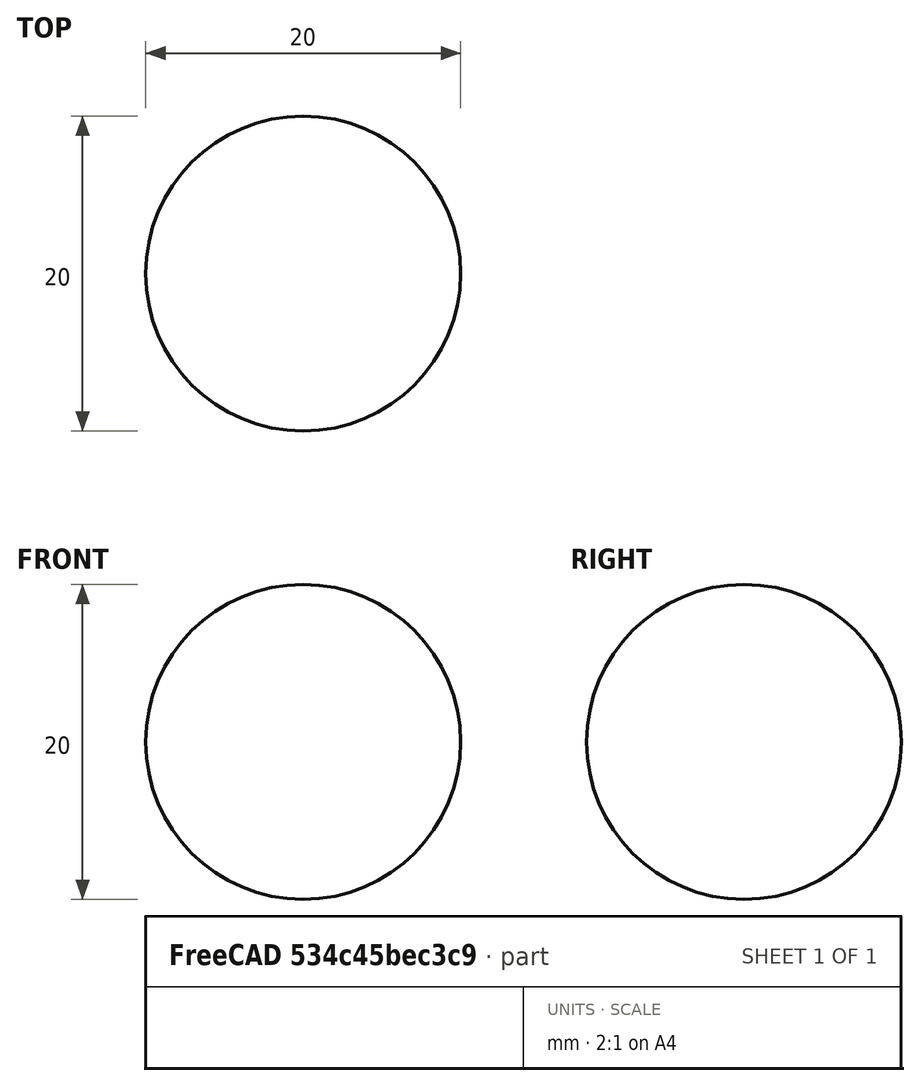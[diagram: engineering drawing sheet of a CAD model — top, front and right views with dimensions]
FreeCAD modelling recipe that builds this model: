
FCSTD DOCUMENT  (FreeCAD 0.18R14555 (Git shallow))
Label: CURVA DE VIVIANI
License: All rights reserved
LicenseURL: http://en.wikipedia.org/wiki/All_rights_reserved
objects: App::DocumentObjectGroupPython×2, Part::Feature×1, Part::Sphere×1
note: 2 computed .brp shape members not serialized (recipe doc carries the construction recipe); baked Part::Feature solids carry a one-line shape summary decoded from their .brp

FEATURE [Part::Feature] Wire
  shape: bbox 100 x 100.2 x 200 mm, 0 faces, 0 solids (baked)
FEATURE [Part::Sphere] Sphere
  Angle1 = -90
  Angle2 = 90
  Angle3 = 360
  AttacherType = Attacher::AttachEngine3D
  Placement = pos=(100,0,0) rot=(0,0,1;0rad)
  Radius = 10
FEATURE [App::DocumentObjectGroupPython] My_Placer  # scripted group (container) (typed FeaturePython)
  Placement = pos=(100,0,0) rot=(0,0,1;0rad)
  RotAxis = (0,0,1)
  RotCenter = (0,0,0)
  arc = 0
  arc0 = 0
  arc1 = 90
  target = -> Sphere
  time = 0
  x = 100*x0
  x0 = 1
  x1 = 200
  y = 100*y0
  y0 = 0
  y1 = 0
  z = 100*z0
  z0 = 0
  z1 = 0
  expr: z0 = sin(time * 360)
  expr: y0 = sin(time * 360) * cos(time * 360)
  expr: x0 = cos(time * 360) ^ 2
FEATURE [App::DocumentObjectGroupPython] My_Manager  # scripted group (container) (typed FeaturePython)
  Group = -> [My_Placer]
  intervall = 400
  sleeptime = 0.02
  start = 0
  step = 0
  text = NO
